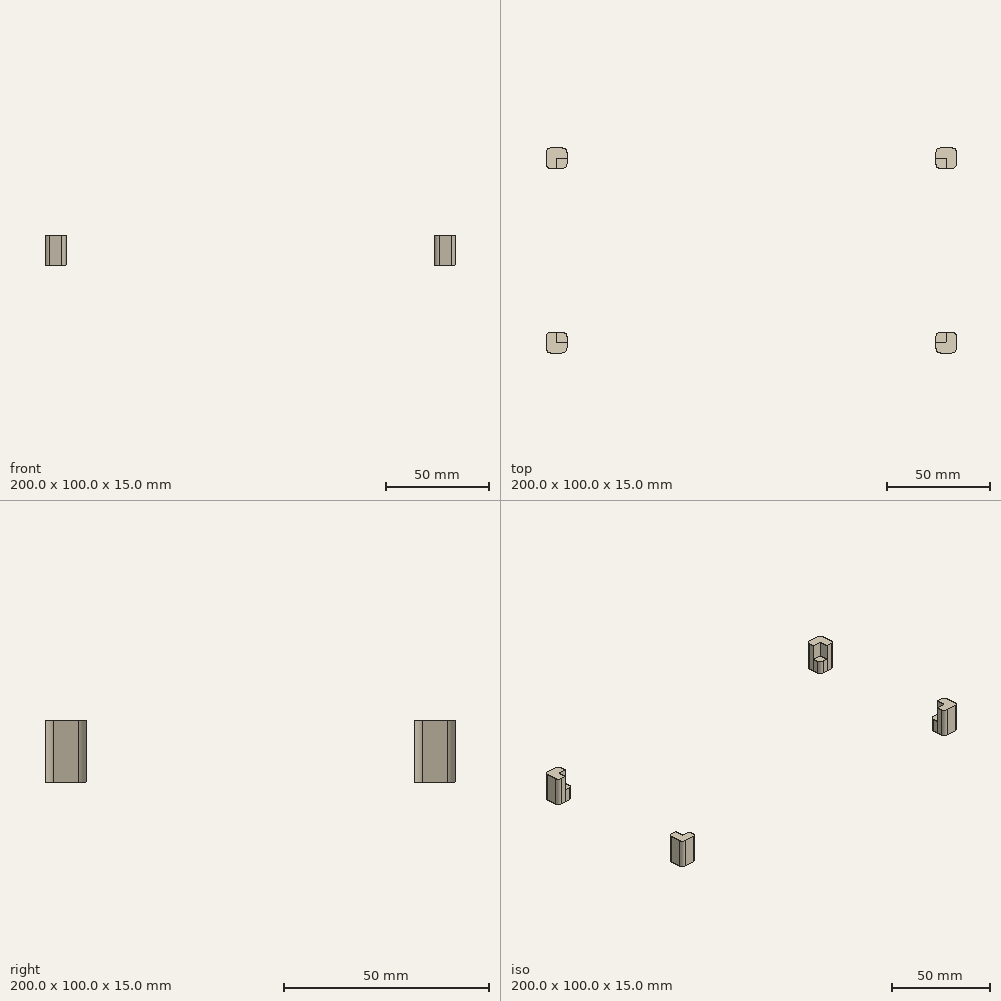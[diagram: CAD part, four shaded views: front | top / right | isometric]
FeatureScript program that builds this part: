
annotation { "Feature Type Name" : "Feature", "Feature Type Description" : "" }
export const myFeature = defineFeature(function(context is Context, id is Id, definition is map)
    precondition{}
    {
        {
            var Q0;
            Q0=qCreatedBy(makeId("Top.planeOp"),FACE);
            var sketch = newSketch(context, id + "F0", { "sketchPlane" : qUnion([Q0])});
            skLineSegment(sketch, "E0.bottom", {"start": v(100, -50) * mm, "end": v(-100, -50) * mm});
            skLineSegment(sketch, "E0.top", {"start": v(100, 50) * mm, "end": v(-100, 50) * mm});
            skLineSegment(sketch, "E0.left", {"start": v(100, -50) * mm, "end": v(100, 50) * mm});
            skLineSegment(sketch, "E0.right", {"start": v(-100, -50) * mm, "end": v(-100, 50) * mm});
            skPoint(sketch, "E0.middle", {"position": v(0, 0) * mm});
            skLineSegment(sketch, "E1.bottom", {"start": v(95, -45) * mm, "end": v(-95, -45) * mm});
            skLineSegment(sketch, "E1.top", {"start": v(95, 45) * mm, "end": v(-95, 45) * mm});
            skLineSegment(sketch, "E1.left", {"start": v(95, -45) * mm, "end": v(95, 45) * mm});
            skLineSegment(sketch, "E1.right", {"start": v(-95, -45) * mm, "end": v(-95, 45) * mm});
            skLineSegment(sketch, "E2.bottom", {"start": v(-100, 50) * mm, "end": v(-90, 50) * mm});
            skLineSegment(sketch, "E2.top", {"start": v(-100, 40) * mm, "end": v(-90, 40) * mm});
            skLineSegment(sketch, "E2.left", {"start": v(-100, 50) * mm, "end": v(-100, 40) * mm});
            skLineSegment(sketch, "E2.right", {"start": v(-90, 50) * mm, "end": v(-90, 40) * mm});
            skLineSegment(sketch, "E3.bottom", {"start": v(100, 50) * mm, "end": v(90, 50) * mm});
            skLineSegment(sketch, "E3.top", {"start": v(100, 40) * mm, "end": v(90, 40) * mm});
            skLineSegment(sketch, "E3.left", {"start": v(100, 50) * mm, "end": v(100, 40) * mm});
            skLineSegment(sketch, "E3.right", {"start": v(90, 50) * mm, "end": v(90, 40) * mm});
            skLineSegment(sketch, "E4.bottom", {"start": v(100, -50) * mm, "end": v(90, -50) * mm});
            skLineSegment(sketch, "E4.top", {"start": v(100, -40) * mm, "end": v(90, -40) * mm});
            skLineSegment(sketch, "E4.left", {"start": v(100, -50) * mm, "end": v(100, -40) * mm});
            skLineSegment(sketch, "E4.right", {"start": v(90, -50) * mm, "end": v(90, -40) * mm});
            skLineSegment(sketch, "E5.bottom", {"start": v(-100, -50) * mm, "end": v(-90, -50) * mm});
            skLineSegment(sketch, "E5.top", {"start": v(-100, -40) * mm, "end": v(-90, -40) * mm});
            skLineSegment(sketch, "E5.left", {"start": v(-100, -50) * mm, "end": v(-100, -40) * mm});
            skLineSegment(sketch, "E5.right", {"start": v(-90, -50) * mm, "end": v(-90, -40) * mm});
            skSolve(sketch);
        }
        {
            var Q0;
            {var subQ7=sQuery(id+"F0.wireOp",EDGE,"E0.right");var subQ8=sQuery(id+"F0.wireOp",EDGE,"E0.top");var subQ9=makeQuery(id+"F0.imprint","INTERSECT",VERTEX,{"derivedFrom":[subQ8,subQ7]});Q0=makeQuery(id+"F0.imprint","IMPRINT",FACE,{"disambiguationData":[TD([[makeQuery(id+"F0.imprint","IMPRINT",EDGE,{"disambiguationData":[TD([[subQ9,1.0]])],"derivedFrom":subQ8}),1.0]])]});}
            var Q1;
            {var subQ7=sQuery(id+"F0.wireOp",EDGE,"E0.right");var subQ9=sQuery(id+"F0.wireOp",EDGE,"E0.bottom");var subQ10=makeQuery(id+"F0.imprint","INTERSECT",VERTEX,{"derivedFrom":[subQ9,subQ7]});Q1=makeQuery(id+"F0.imprint","IMPRINT",FACE,{"disambiguationData":[TD([[makeQuery(id+"F0.imprint","IMPRINT",EDGE,{"disambiguationData":[TD([[subQ10,1.0]])],"derivedFrom":subQ9}),-1.0]])]});}
            var Q2;
            {var subQ0=sQuery(id+"F0.wireOp",EDGE,"E3.right");var subQ6=sQuery(id+"F0.wireOp",EDGE,"E0.top");var subQ11=makeQuery(id+"F0.imprint","INTERSECT",VERTEX,{"derivedFrom":[subQ6,subQ0]});Q2=makeQuery(id+"F0.imprint","IMPRINT",FACE,{"disambiguationData":[TD([[makeQuery(id+"F0.imprint","IMPRINT",EDGE,{"disambiguationData":[TD([[subQ11,1.0]])],"derivedFrom":subQ6}),1.0]])]});}
            var Q3;
            {var subQ5=sQuery(id+"F0.wireOp",EDGE,"E4.right");var subQ9=sQuery(id+"F0.wireOp",EDGE,"E0.bottom");var subQ11=makeQuery(id+"F0.imprint","INTERSECT",VERTEX,{"derivedFrom":[subQ9,subQ5]});Q3=makeQuery(id+"F0.imprint","IMPRINT",FACE,{"disambiguationData":[TD([[makeQuery(id+"F0.imprint","IMPRINT",EDGE,{"disambiguationData":[TD([[subQ11,1.0]])],"derivedFrom":subQ9}),-1.0]])]});}
            extrude(context, id + "F1", {"entities" : qUnion([Q0, Q1, Q2, Q3]), "depth" : 15 * mm, "offsetDistance" : 25 * mm});
        }
        {
            var Q0;
            {var subQ0=sQuery(id+"F0.wireOp",EDGE,"E1.right");var subQ1=sQuery(id+"F0.wireOp",EDGE,"E1.bottom");var subQ2=makeQuery(id+"F0.imprint","INTERSECT",VERTEX,{"derivedFrom":[subQ1,subQ0]});Q0=makeQuery(id+"F0.imprint","IMPRINT",FACE,{"disambiguationData":[TD([[makeQuery(id+"F0.imprint","IMPRINT",EDGE,{"disambiguationData":[TD([[subQ2,1.0]])],"derivedFrom":subQ1}),-1.0]])]});}
            var Q1;
            {var subQ0=sQuery(id+"F0.wireOp",EDGE,"E1.right");var subQ1=sQuery(id+"F0.wireOp",EDGE,"E1.top");var subQ2=makeQuery(id+"F0.imprint","INTERSECT",VERTEX,{"derivedFrom":[subQ1,subQ0]});Q1=makeQuery(id+"F0.imprint","IMPRINT",FACE,{"disambiguationData":[TD([[makeQuery(id+"F0.imprint","IMPRINT",EDGE,{"disambiguationData":[TD([[subQ2,1.0]])],"derivedFrom":subQ1}),1.0]])]});}
            var Q2;
            {var subQ0=sQuery(id+"F0.wireOp",EDGE,"E3.right");var subQ1=sQuery(id+"F0.wireOp",EDGE,"E1.top");var subQ2=makeQuery(id+"F0.imprint","INTERSECT",VERTEX,{"derivedFrom":[subQ1,subQ0]});Q2=makeQuery(id+"F0.imprint","IMPRINT",FACE,{"disambiguationData":[TD([[makeQuery(id+"F0.imprint","IMPRINT",EDGE,{"disambiguationData":[TD([[subQ2,1.0]])],"derivedFrom":subQ1}),1.0]])]});}
            var Q3;
            {var subQ0=sQuery(id+"F0.wireOp",EDGE,"E4.right");var subQ1=sQuery(id+"F0.wireOp",EDGE,"E1.bottom");var subQ2=makeQuery(id+"F0.imprint","INTERSECT",VERTEX,{"derivedFrom":[subQ1,subQ0]});Q3=makeQuery(id+"F0.imprint","IMPRINT",FACE,{"disambiguationData":[TD([[makeQuery(id+"F0.imprint","IMPRINT",EDGE,{"disambiguationData":[TD([[subQ2,1.0]])],"derivedFrom":subQ1}),-1.0]])]});}
            extrude(context, id + "F2", {"entities" : qUnion([Q0, Q1, Q2, Q3]), "depth" : 7 * mm, "offsetDistance" : 25 * mm});
        }
        {
            var Q0;
            Q0=makeQuery(id+"F1.opExtrude","SWEPT_EDGE",EDGE,{"disambiguationData":[OSD([sQuery(id+"F0.wireOp",EDGE,"E0.right"),sQuery(id+"F0.wireOp",EDGE,"E2.top")])]});
            var Q1;
            Q1=makeQuery(id+"F1.opExtrude","SWEPT_EDGE",EDGE,{"disambiguationData":[OSD([sQuery(id+"F0.wireOp",EDGE,"E0.top"),sQuery(id+"F0.wireOp",EDGE,"E2.right")])]});
            fillet(context, id + "F3", {"entities" : qUnion([Q0, Q1]), "radius" : 2 * mm, "tangentPropagation" : true, "allowEdgeOverflow" : false});
        }
        {
            var Q0;
            Q0=makeQuery(id+"F1.opExtrude","SWEPT_EDGE",EDGE,{"disambiguationData":[OSD([sQuery(id+"F0.wireOp",EDGE,"E0.top"),sQuery(id+"F0.wireOp",EDGE,"E0.right")])]});
            var Q1;
            Q1=makeQuery(id+"F2.opExtrude","SWEPT_EDGE",EDGE,{"disambiguationData":[OSD([sQuery(id+"F0.wireOp",EDGE,"E2.top"),sQuery(id+"F0.wireOp",EDGE,"E2.right")])]});
            var Q2;
            Q2=makeQuery(id+"F1.opExtrude","SWEPT_EDGE",EDGE,{"disambiguationData":[OSD([sQuery(id+"F0.wireOp",EDGE,"E0.left"),sQuery(id+"F0.wireOp",EDGE,"E3.top")])]});
            var Q3;
            Q3=makeQuery(id+"F2.opExtrude","SWEPT_EDGE",EDGE,{"disambiguationData":[OSD([sQuery(id+"F0.wireOp",EDGE,"E3.top"),sQuery(id+"F0.wireOp",EDGE,"E3.right")])]});
            var Q4;
            Q4=makeQuery(id+"F1.opExtrude","SWEPT_EDGE",EDGE,{"disambiguationData":[OSD([sQuery(id+"F0.wireOp",EDGE,"E0.top"),sQuery(id+"F0.wireOp",EDGE,"E0.left")])]});
            var Q5;
            Q5=makeQuery(id+"F1.opExtrude","SWEPT_EDGE",EDGE,{"disambiguationData":[OSD([sQuery(id+"F0.wireOp",EDGE,"E0.top"),sQuery(id+"F0.wireOp",EDGE,"E3.right")])]});
            var Q6;
            Q6=makeQuery(id+"F2.opExtrude","SWEPT_EDGE",EDGE,{"disambiguationData":[OSD([sQuery(id+"F0.wireOp",EDGE,"E4.top"),sQuery(id+"F0.wireOp",EDGE,"E4.right")])]});
            var Q7;
            Q7=makeQuery(id+"F1.opExtrude","SWEPT_EDGE",EDGE,{"disambiguationData":[OSD([sQuery(id+"F0.wireOp",EDGE,"E0.bottom"),sQuery(id+"F0.wireOp",EDGE,"E4.right")])]});
            var Q8;
            Q8=makeQuery(id+"F1.opExtrude","SWEPT_EDGE",EDGE,{"disambiguationData":[OSD([sQuery(id+"F0.wireOp",EDGE,"E0.bottom"),sQuery(id+"F0.wireOp",EDGE,"E0.left")])]});
            var Q9;
            Q9=makeQuery(id+"F1.opExtrude","SWEPT_EDGE",EDGE,{"disambiguationData":[OSD([sQuery(id+"F0.wireOp",EDGE,"E0.left"),sQuery(id+"F0.wireOp",EDGE,"E4.top")])]});
            fillet(context, id + "F4", {"entities" : qUnion([Q0, Q1, Q2, Q3, Q4, Q5, Q6, Q7, Q8, Q9]), "radius" : 2 * mm, "tangentPropagation" : true, "allowEdgeOverflow" : false});
        }
        {
            var Q0;
            Q0=makeQuery(id+"F1.opExtrude","SWEPT_EDGE",EDGE,{"disambiguationData":[OSD([sQuery(id+"F0.wireOp",EDGE,"E0.bottom"),sQuery(id+"F0.wireOp",EDGE,"E5.right")])]});
            var Q1;
            Q1=makeQuery(id+"F1.opExtrude","SWEPT_EDGE",EDGE,{"disambiguationData":[OSD([sQuery(id+"F0.wireOp",EDGE,"E0.bottom"),sQuery(id+"F0.wireOp",EDGE,"E0.right")])]});
            var Q2;
            Q2=makeQuery(id+"F1.opExtrude","SWEPT_EDGE",EDGE,{"disambiguationData":[OSD([sQuery(id+"F0.wireOp",EDGE,"E0.right"),sQuery(id+"F0.wireOp",EDGE,"E5.top")])]});
            var Q3;
            Q3=makeQuery(id+"F2.opExtrude","SWEPT_EDGE",EDGE,{"disambiguationData":[OSD([sQuery(id+"F0.wireOp",EDGE,"E5.top"),sQuery(id+"F0.wireOp",EDGE,"E5.right")])]});
            fillet(context, id + "F5", {"entities" : qUnion([Q0, Q1, Q2, Q3]), "radius" : 2 * mm, "tangentPropagation" : true, "allowEdgeOverflow" : false});
        }
    });
